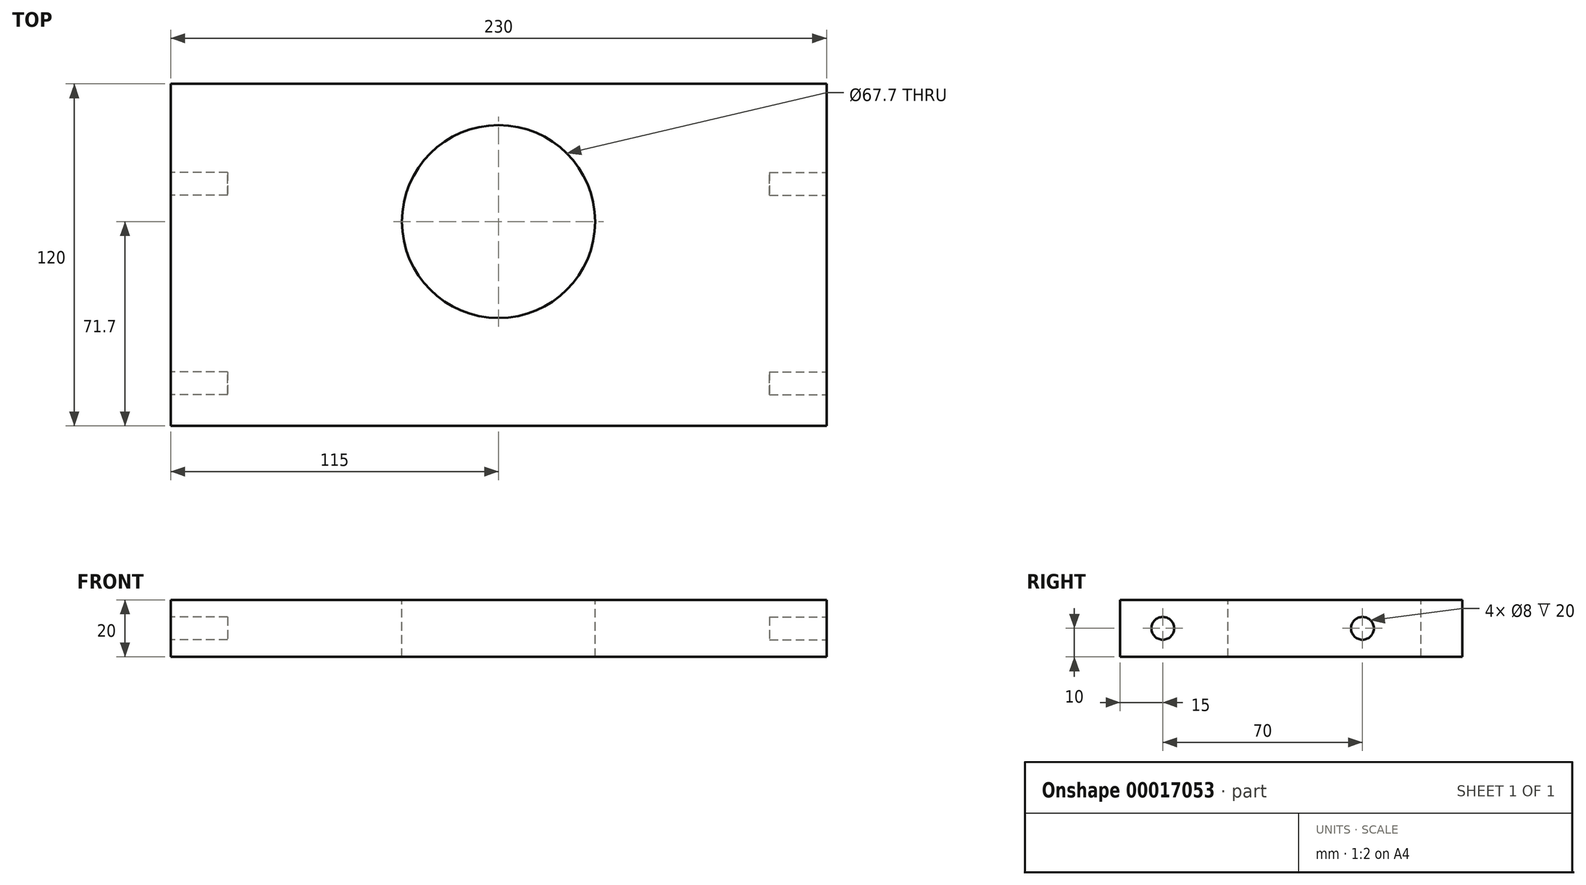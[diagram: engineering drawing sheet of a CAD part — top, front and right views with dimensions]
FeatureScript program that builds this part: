
annotation { "Feature Type Name" : "Feature", "Feature Type Description" : "" }
export const myFeature = defineFeature(function(context is Context, id is Id, definition is map)
    precondition{}
    {
        {
            var Q0;
            Q0=qCreatedBy(makeId("Top.planeOp"),FACE);
            var sketch = newSketch(context, id + "F0", { "sketchPlane" : qUnion([Q0])});
            skLineSegment(sketch, "E0.bottom", {"start": v(115, 70) * mm, "end": v(-115, 70) * mm});
            skLineSegment(sketch, "E0.top", {"start": v(115, -50) * mm, "end": v(-115, -50) * mm});
            skLineSegment(sketch, "E0.left", {"start": v(115, 70) * mm, "end": v(115, -50) * mm});
            skLineSegment(sketch, "E0.right", {"start": v(-115, 70) * mm, "end": v(-115, -50) * mm});
            skSolve(sketch);
        }
        {
            var Q0;
            Q0 = qSketchRegion(id + "F0", true);
            extrude(context, id + "F1", {"entities" : qUnion([Q0]), "depth" : 20 * mm});
        }
        {
            var Q0;
            Q0=makeQuery(id+"F1.opExtrude","SWEPT_FACE",FACE,{"disambiguationData":[OSD([sQuery(id+"F0.wireOp",EDGE,"E0.right")])]});
            var sketch = newSketch(context, id + "F2", { "sketchPlane" : qUnion([Q0])});
            skCircle(sketch, "E1", {"center": v(-35, 10) * mm, "radius": 4 * mm});
            skCircle(sketch, "E2", {"center": v(35, 10) * mm, "radius": 4 * mm});
            skSolve(sketch);
        }
        {
            var Q0;
            Q0 = qSketchRegion(id + "F2", true);
            extrude(context, id + "F3", {"entities" : qUnion([Q0]), "operationType" : NewBodyOperationType.REMOVE, "oppositeDirection" : true, "depth" : 20 * mm});
        }
        {
            var Q0;
            Q0=makeQuery(id+"F1.opExtrude","CAP_FACE",FACE,{"disambiguationData":[OSD([sQuery(id+"F0.wireOp",EDGE,"E0.bottom"),sQuery(id+"F0.wireOp",EDGE,"E0.top"),sQuery(id+"F0.wireOp",EDGE,"E0.left"),sQuery(id+"F0.wireOp",EDGE,"E0.right")])],"isStart":false});
            var sketch = newSketch(context, id + "F4", { "sketchPlane" : qUnion([Q0])});
            skCircle(sketch, "E3", {"center": v(0, 21.7) * mm, "radius": 33.85 * mm});
            skSolve(sketch);
        }
        {
            var Q0;
            Q0 = qSketchRegion(id + "F4", true);
            extrude(context, id + "F5", {"entities" : qUnion([Q0]), "operationType" : NewBodyOperationType.REMOVE, "endBound" : BoundingType.THROUGH_ALL, "oppositeDirection" : true, "depth" : 25 * mm});
        }
        {
            var Q0;
            Q0=makeQuery(id+"F1.opExtrude","CAP_FACE",FACE,{"disambiguationData":[OSD([sQuery(id+"F0.wireOp",EDGE,"E0.bottom"),sQuery(id+"F0.wireOp",EDGE,"E0.top"),sQuery(id+"F0.wireOp",EDGE,"E0.left"),sQuery(id+"F0.wireOp",EDGE,"E0.right")])],"isStart":false});
            var sketch = newSketch(context, id + "F6", { "sketchPlane" : qUnion([Q0])});
            skLineSegment(sketch, "E4.bottom", {"start": v(115, -50) * mm, "end": v(0, -50) * mm});
            skLineSegment(sketch, "E4.top", {"start": v(115, 70) * mm, "end": v(0, 70) * mm});
            skLineSegment(sketch, "E4.left", {"start": v(115, -50) * mm, "end": v(115, 70) * mm});
            skLineSegment(sketch, "E4.right", {"start": v(0, -50) * mm, "end": v(0, 70) * mm});
            skSolve(sketch);
        }
        {
            var Q0;
            Q0 = qSketchRegion(id + "F6", true);
            extrude(context, id + "F7", {"entities" : qUnion([Q0]), "operationType" : NewBodyOperationType.REMOVE, "endBound" : BoundingType.THROUGH_ALL, "oppositeDirection" : true, "depth" : 25 * mm});
        }
        {
            var Q0;
            Q0=makeQuery(id+"F1.opExtrude","SWEPT_BODY",BODY,{"disambiguationData":[OSD([sQuery(id+"F0.wireOp",EDGE,"E0.bottom"),sQuery(id+"F0.wireOp",EDGE,"E0.top"),sQuery(id+"F0.wireOp",EDGE,"E0.left"),sQuery(id+"F0.wireOp",EDGE,"E0.right")])]});
            var Q1;
            Q1=qCreatedBy(makeId("Right.planeOp"),FACE);
            mirror(context, id + "F8", {"operationType" : NewBodyOperationType.ADD, "entities" : qUnion([Q0]), "mirrorPlane" : qUnion([Q1])});
        }
    });
